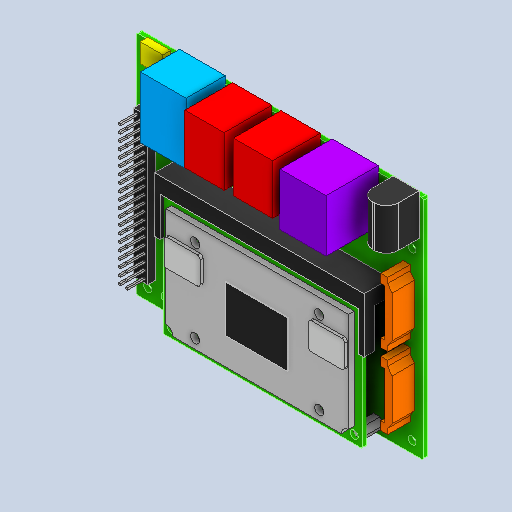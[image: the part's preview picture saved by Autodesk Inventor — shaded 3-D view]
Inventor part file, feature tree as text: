
AUTODESK INVENTOR PART (.ipt)
format: ipt  version: 2024.2 (Build 282272000, 272)  size: 650,240 bytes
history: native  units: mm
features: extrude x20, sketch x7, other x6, fillet x4, pattern_linear x1
ambient origin geometry x8: Origin, YZ Plane, XZ Plane, XY Plane, X Axis, Y Axis, Z Axis, Center Point
bodies: Solid1 (feature_tree), Solid2 (feature_tree), Solid3 (feature_tree), Solid4 (feature_tree), Solid5 (feature_tree), Solid6 (feature_tree), Solid8 (feature_tree), Solid9 (feature_tree), Solid10 (feature_tree)
feature tree (38):
  extrude  "Extrusion1"  Depth=79.0mm
  extrude  "Extrusion2"  Depth=6.0mm
  fillet  "Fillet1"  Radius=2.75mm
  extrude  "Extrusion3"  Depth=2.75mm
  extrude  "Extrusion4"  Depth=4.0mm
  pattern_linear  "Rectangular Pattern1"  Spacing1=0.6mm  [1 undecoded]
  extrude  "Extrusion5"  Depth=1.46mm
  extrude  "Extrusion6"  Depth=7.46mm
  extrude  "Extrusion7"  Depth=5.08mm
  fillet  "Fillet2"  Radius=50.8mm
  extrude  "Extrusion8"  Depth=2.54mm TaperAngle=0.0deg
  extrude  "Extrusion9"  Depth=0.64mm
  extrude  "Extrusion10"  Depth=0.64mm
  extrude  "Extrusion11"  Depth=0.95mm
  fillet  "Fillet3"  Radius=0.95mm
  extrude  "Extrusion12"  Depth=6.06mm TaperAngle=0.0deg
  extrude  "Extrusion13"  Depth=2.54mm
  extrude  "Extrusion14"  Depth=2.54mm
  extrude  "Extrusion15"  Depth=2.75mm
  extrude  "Extrusion16"  Depth=2.75mm
  extrude  "Extrusion17"  Depth=20.2mm
  extrude  "Extrusion18"  Depth=16.2mm
  extrude  "Extrusion19"  Depth=3.6mm
  extrude  "Extrusion20"  Depth=3.6mm
  fillet  "Fillet4"  Radius=4.0mm
  sketch  "Sketch2"  dims[d0=100.0mm d1=79.0mm]
  sketch  "Sketch5"  dims[d2=1.57mm d3=0.0mm d4=6.0mm d5=2.75mm]
  sketch  "Sketch9"  dims[d6=2.75mm d7=2.75mm]
  sketch  "Sketch12"  dims[d8=4.0mm d9=17.0mm]
  sketch  "Sketch13"  dims[d10=29.0mm]
  other  "CAMERA_CONNECTORS"
  sketch  "Sketch16"  dims[d11=4.0mm]
  other  "USB_MINI"
  other  "ETHERNET"
  sketch  "Sketch19"  dims[d12=0.0mm d13=0.0mm d14=0.6mm d15=1.46mm d16=7.46mm d17=5.08mm d18=50.8mm d19=2.54mm d20=0.0mm d21=0.64mm d22=0.64mm d23=0.95mm d24=0.95mm d25=6.06mm d26=0.0mm d27=200.0mm d29=2.54mm d30=20.0mm d32=2.54mm d33=2.75mm d34=2.75mm d35=20.2mm d36=16.2mm d37=3.6mm d38=3.6mm d39=4.0mm d40=4.0mm d41=6.69mm d42=0.0mm d43=5.5mm d44=73.0mm d45=63.6mm d46=31.8mm d47=45.45mm d48=9.15mm d49=0.0mm d50=69.6mm d51=0.75mm d52=3.0mm d53=1.2mm d54=0.0mm d55=0.6mm d56=1.26mm d57=1.26mm d58=2.0mm d59=36.5mm d60=73.0mm d61=13.7mm d62=0.0mm d63=5.0mm d64=5.0mm d65=2.7mm d66=2.7mm d67=2.0mm d68=0.0mm d69=21.6mm d70=16.14mm d71=28.67mm d72=24.0mm d73=0.245mm d74=0.0mm d75=15.95mm d76=32.7mm d77=12.6mm d78=9.4mm d79=10.8mm d80=1.0mm d81=0.0mm d82=1.0mm d83=3.2mm d84=13.2mm d85=35.0mm d86=3.2mm d87=6.2mm d88=13.2mm d89=10.8mm d90=0.0mm d91=0.0mm d92=22.4mm d93=22.4mm d94=3.9mm d95=3.9mm d96=2.6mm d97=9.3mm d98=3.15mm d99=7.776mm d100=0.0mm d101=2.5mm d102=2.5mm d103=3.0mm d104=3.0mm d105=3.0mm d106=3.0mm d107=3.0mm d108=0.0mm d109=25.307274mm d110=25.307274mm d111=4.0mm d112=4.0mm d113=1.5mm d114=2.6mm d115=1.3mm d116=3.0mm d117=0.0mm d118=8.0mm d119=6.6mm d120=6.0mm d121=4.0mm d122=2.7mm d123=0.0mm d124=15.1mm d125=18.85mm d126=21.35mm d127=15.9mm d128=13.65mm d129=0.0mm d130=13.65mm d131=17.4mm d132=33.525mm d133=15.75mm d134=1.625mm d135=16.566mm d136=0.0mm d137=16.06mm d138=18.25mm d139=15.715mm d140=16.225mm d141=18.176mm d142=0.0mm d143=9.0mm d144=14.4mm d145=1.5mm d146=11.4mm d147=0.0mm d148=12.9mm d149=4.25mm]
  other  "USB"
  other  "HDMI_DISPLAYPORT"
  other  "DC_JACK"
note: 1 required parameter value undecoded (feature->parameter linkage not recoverable at this tier; creation-order binding heuristic only, values carry confidence <= 0.55)
